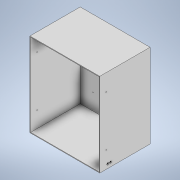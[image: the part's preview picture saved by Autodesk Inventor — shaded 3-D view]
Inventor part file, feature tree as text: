
AUTODESK INVENTOR PART (.ipt)
format: ipt  version: 2020 (Build 240168000, 168)  size: 194,560 bytes
history: native  units: mm
features: extrude x5, sketch x5, shell x1, mirror x1
ambient origin geometry x8: Origin, YZ Plane, XZ Plane, XY Plane, X Axis, Y Axis, Z Axis, Center Point
bodies: Solid1 (feature_tree)
feature tree (12):
  extrude  "Base"  Depth=600.0mm
  shell  "Shell1"  Thickness=360.0mm
  extrude  "Cable Holes"  Depth=5.0mm
  extrude  "Mount Holes inner walls"  Depth=28.75mm
  extrude  "Extrusion5"  Depth=10.0mm
  mirror  "Mirror2"
  extrude  "Fan holes"  Depth=10.0mm
  sketch  "Sketch2"  dims[d0=500.0mm d1=600.0mm d2=360.0mm d3=0.0mm]
  sketch  "Sketch4"  dims[d4=5.0mm d18=15.0mm]
  sketch  "Sketch5"  dims[d19=57.5mm d20=28.75mm]
  sketch  "Sketch6"  dims[d21=20.0mm d23=20.0mm d24=10.0mm d26=10.0mm]
  sketch  "Sketch7"  dims[d28=10.0mm d29=0.0mm d30=309.5mm d31=359.5mm d32=5.5mm d33=20.0mm d35=309.5mm d36=20.0mm d38=359.5mm d41=10.0mm d42=0.0mm d43=5.25mm d44=359.5mm d46=5.25mm d47=340.0mm d48=0.0mm d49=4.3mm d50=20.0mm d52=32.0mm d53=20.0mm d55=32.0mm d58=38.0mm d59=59.0mm d60=45.0deg d61=10.0mm d62=0.0mm d63=309.25mm]
